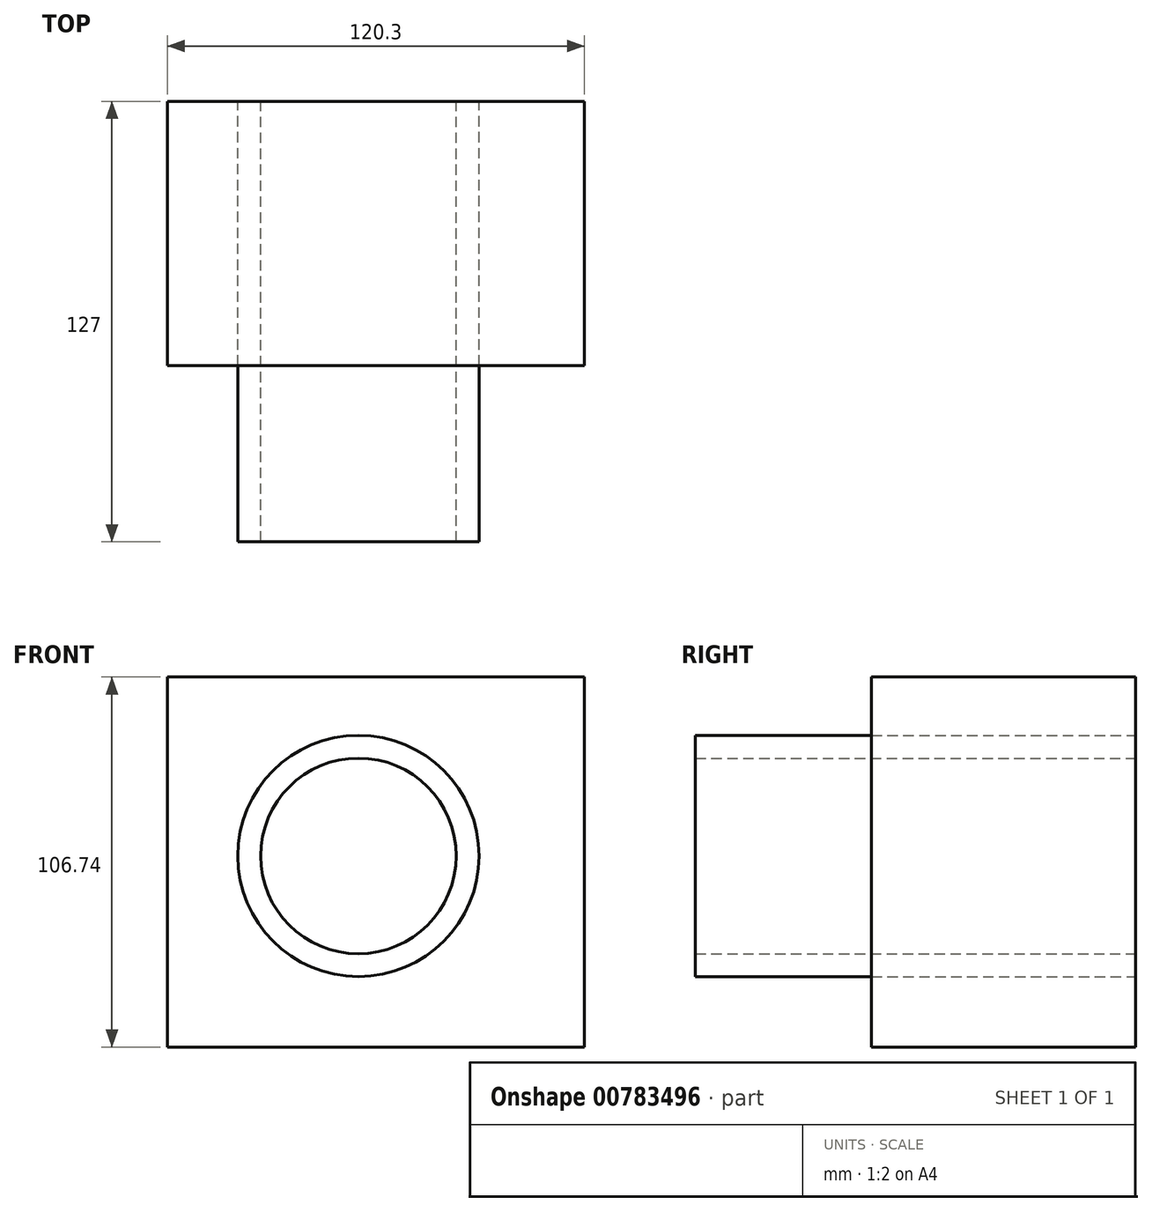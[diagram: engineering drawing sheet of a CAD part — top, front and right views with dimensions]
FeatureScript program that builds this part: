
annotation { "Feature Type Name" : "Feature", "Feature Type Description" : "" }
export const myFeature = defineFeature(function(context is Context, id is Id, definition is map)
    precondition{}
    {
        {
            var Q0;
            Q0=qCreatedBy(makeId("Front.planeOp"),FACE);
            var sketch = newSketch(context, id + "F0", { "sketchPlane" : qUnion([Q0])});
            skLineSegment(sketch, "E0.bottom", {"start": v(-55.1, 51.63) * mm, "end": v(65.2, 51.63) * mm});
            skLineSegment(sketch, "E0.top", {"start": v(-55.1, -55.1) * mm, "end": v(65.2, -55.1) * mm});
            skLineSegment(sketch, "E0.left", {"start": v(-55.1, 51.63) * mm, "end": v(-55.1, -55.1) * mm});
            skLineSegment(sketch, "E0.right", {"start": v(65.2, 51.63) * mm, "end": v(65.2, -55.1) * mm});
            skCircle(sketch, "E1", {"center": v(0, 0) * mm, "radius": 34.8 * mm});
            skCircle(sketch, "E2", {"center": v(0, 0) * mm, "radius": 28.21 * mm});
            skSolve(sketch);
        }
        {
            var Q0;
            Q0 = qSketchRegion(id + "F0", true);
            extrude(context, id + "F1", {"entities" : qUnion([Q0]), "depth" : 76.2 * mm, "offsetDistance" : 25.4 * mm});
        }
        {
            var Q0;
            Q0=makeQuery(id+"F0.imprint","IMPRINT",FACE,{"disambiguationData":[TD([[makeQuery(id+"F0.imprint","IMPRINT",EDGE,{"derivedFrom":sQuery(id+"F0.wireOp",EDGE,"E1")}),1.0]])]});
            extrude(context, id + "F2", {"entities" : qUnion([Q0]), "depth" : 127 * mm, "offsetDistance" : 25.4 * mm});
        }
    });
